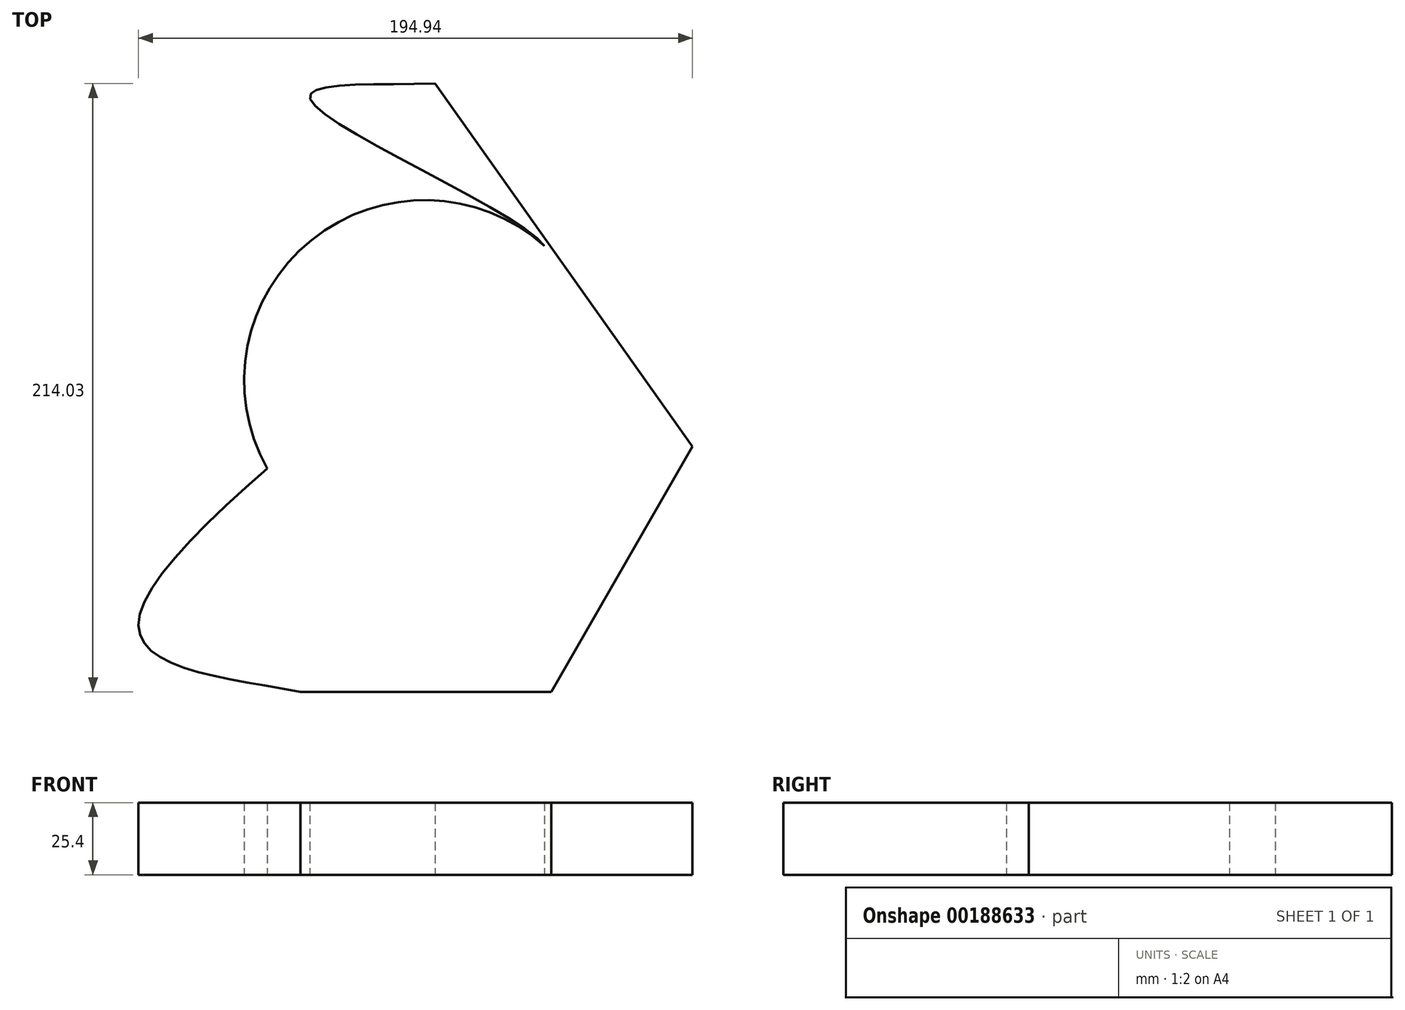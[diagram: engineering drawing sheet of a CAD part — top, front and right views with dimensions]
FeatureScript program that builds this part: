
annotation { "Feature Type Name" : "Feature", "Feature Type Description" : "" }
export const myFeature = defineFeature(function(context is Context, id is Id, definition is map)
    precondition{}
    {
        {
            var Q0;
            Q0=qCreatedBy(makeId("Top.planeOp"),FACE);
            var sketch = newSketch(context, id + "F0", { "sketchPlane" : qUnion([Q0])});
            skCircle(sketch, "E0", {"center": v(43.64, 23.27) * mm, "radius": 63.46 * mm});
            skLineSegment(sketch, "E1", {"start": v(47.37, 127.75) * mm, "end": v(137.92, 0) * mm});
            skLineSegment(sketch, "E2", {"start": v(137.92, 0) * mm, "end": v(88.22, -86.28) * mm});
            skLineSegment(sketch, "E3", {"start": v(88.22, -86.28) * mm, "end": v(0, -86.28) * mm});
            skPoint(sketch, "E4.start.orphan", {"position": v(0, 93.23) * mm});
            skFitSpline(sketch, "E5", {"points": [v(47.37, 127.75) * mm, v(3.7, 121.75) * mm, v(85.84, 70.66) * mm, v(86.1, 65.94) * mm, v(85.6, 65.5) * mm, v(-56.33, -58.2) * mm, v(0, -86.28) * mm], "startDerivative": vector(-420.82, -10.3) * mm, "endDerivative": vector(461.5, -84.04) * mm});
            skSolve(sketch);
        }
        {
            var Q0;
            Q0 = qSketchRegion(id + "F0", true);
            extrude(context, id + "F1", {"entities" : qUnion([Q0]), "depth" : 25.4 * mm});
        }
    });
